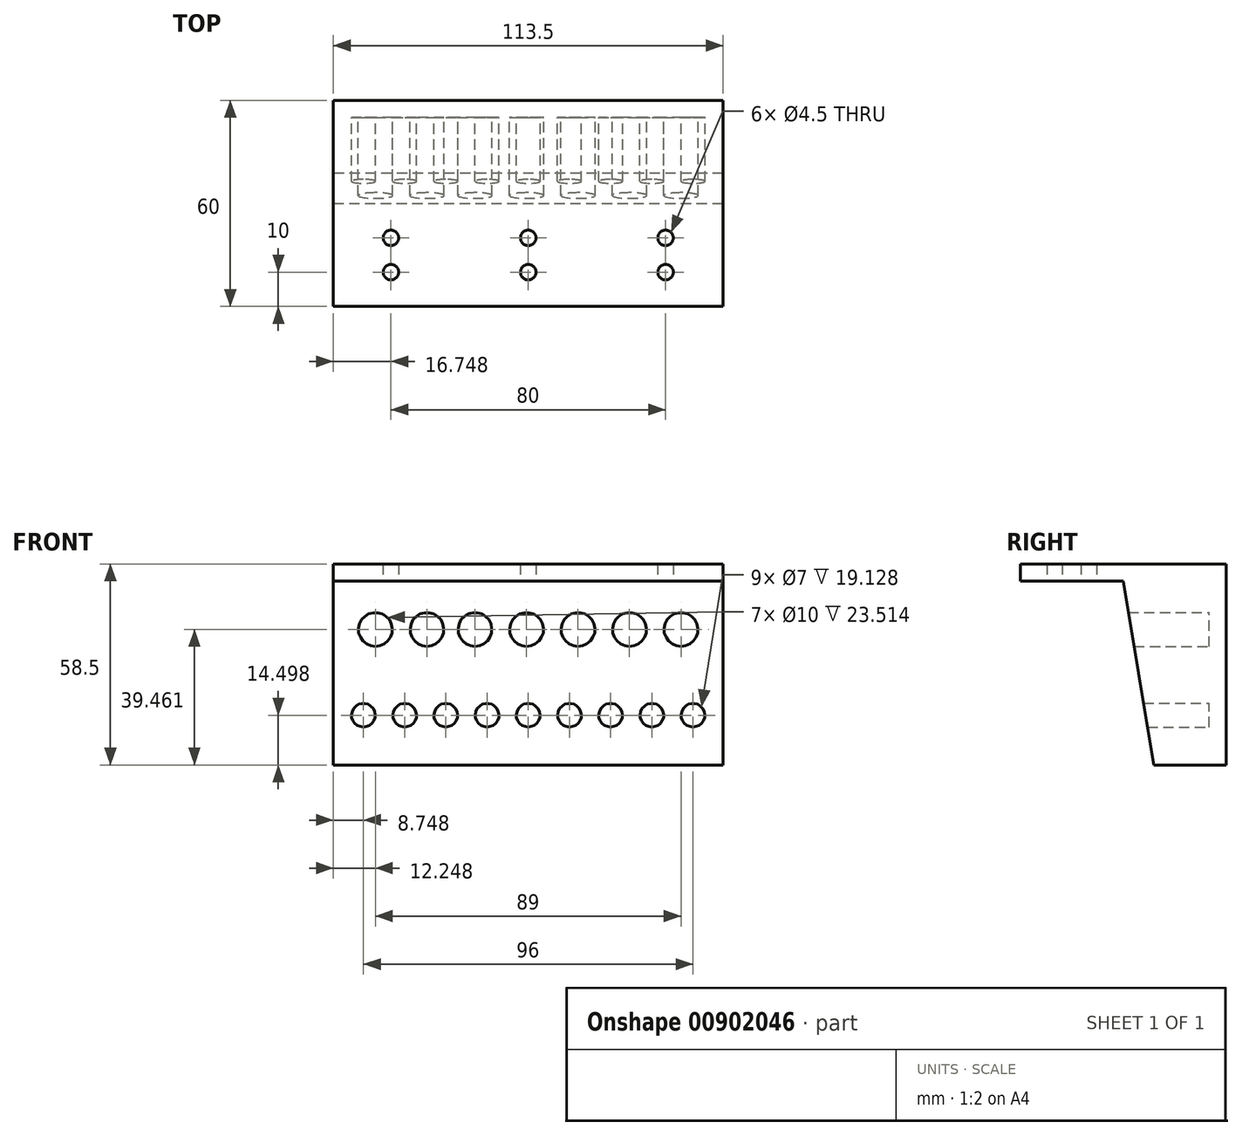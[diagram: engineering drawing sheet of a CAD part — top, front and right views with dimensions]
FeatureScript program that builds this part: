
annotation { "Feature Type Name" : "Feature", "Feature Type Description" : "" }
export const myFeature = defineFeature(function(context is Context, id is Id, definition is map)
    precondition{}
    {
        {
            var Q0;
            Q0=qCreatedBy(makeId("Front.planeOp"),FACE);
            var sketch = newSketch(context, id + "F0", { "sketchPlane" : qUnion([Q0])});
            skLineSegment(sketch, "E0.bottom", {"start": v(-82.73, 51.75) * mm, "end": v(30.77, 51.75) * mm});
            skLineSegment(sketch, "E0.top", {"start": v(-82.73, -1.75) * mm, "end": v(30.77, -1.75) * mm});
            skLineSegment(sketch, "E0.left", {"start": v(-82.73, 51.75) * mm, "end": v(-82.73, -1.75) * mm});
            skLineSegment(sketch, "E0.right", {"start": v(30.77, 51.75) * mm, "end": v(30.77, -1.75) * mm});
            skLineSegment(sketch, "E1", {"start": v(30.77, 37.71) * mm, "end": v(-82.73, 37.71) * mm});
            skLineSegment(sketch, "E2", {"start": v(-82.73, 37.71) * mm, "end": v(-82.73, 12.75) * mm});
            skLineSegment(sketch, "E3", {"start": v(-82.73, 12.75) * mm, "end": v(30.77, 12.75) * mm});
            skCircle(sketch, "E4", {"center": v(18.52, 37.71) * mm, "radius": 5 * mm});
            skCircle(sketch, "E5", {"center": v(3.52, 37.71) * mm, "radius": 5 * mm});
            skCircle(sketch, "E6", {"center": v(-11.48, 37.71) * mm, "radius": 5 * mm});
            skCircle(sketch, "E7", {"center": v(-26.48, 37.71) * mm, "radius": 5 * mm});
            skCircle(sketch, "E8", {"center": v(-41.48, 37.71) * mm, "radius": 5 * mm});
            skCircle(sketch, "E9", {"center": v(-55.48, 37.71) * mm, "radius": 5 * mm});
            skCircle(sketch, "E10", {"center": v(-70.48, 37.71) * mm, "radius": 5 * mm});
            skCircle(sketch, "E11", {"center": v(22.02, 12.75) * mm, "radius": 3.5 * mm});
            skCircle(sketch, "E12", {"center": v(10.02, 12.75) * mm, "radius": 3.5 * mm});
            skCircle(sketch, "E13", {"center": v(-1.98, 12.75) * mm, "radius": 3.5 * mm});
            skCircle(sketch, "E14", {"center": v(-13.98, 12.75) * mm, "radius": 3.5 * mm});
            skCircle(sketch, "E15", {"center": v(-25.98, 12.75) * mm, "radius": 3.5 * mm});
            skCircle(sketch, "E16", {"center": v(-37.98, 12.75) * mm, "radius": 3.5 * mm});
            skCircle(sketch, "E17", {"center": v(-49.98, 12.75) * mm, "radius": 3.5 * mm});
            skCircle(sketch, "E18", {"center": v(-61.98, 12.75) * mm, "radius": 3.5 * mm});
            skCircle(sketch, "E19", {"center": v(-73.98, 12.75) * mm, "radius": 3.5 * mm});
            skSolve(sketch);
        }
        {
            var Q0;
            {var subQ24=sQuery(id+"F0.wireOp",EDGE,"E0.left");var subQ32=sQuery(id+"F0.wireOp",EDGE,"E1");var subQ33=makeQuery(id+"F0.imprint","INTERSECT",VERTEX,{"derivedFrom":[subQ24,subQ32]});var subQ74=sQuery(id+"F0.wireOp",EDGE,"E0.top");var subQ75=sQuery(id+"F0.wireOp",EDGE,"E0.bottom");Q0=qUnion([makeQuery(id+"F0.imprint","IMPRINT",FACE,{"disambiguationData":[TD([[makeQuery(id+"F0.imprint","IMPRINT",EDGE,{"derivedFrom":subQ75}),-1.0]])]}),makeQuery(id+"F0.imprint","IMPRINT",FACE,{"disambiguationData":[TD([[makeQuery(id+"F0.imprint","IMPRINT",EDGE,{"derivedFrom":subQ74}),1.0]])]}),makeQuery(id+"F0.imprint","IMPRINT",FACE,{"disambiguationData":[TD([[makeQuery(id+"F0.imprint","IMPRINT",EDGE,{"disambiguationData":[TD([[subQ33,-1.0]])],"derivedFrom":subQ24}),1.0]])]})]);}
            extrude(context, id + "F1", {"entities" : qUnion([Q0]), "depth" : 25 * mm, "offsetDistance" : 25 * mm});
        }
        {
            var Q0;
            Q0=makeQuery(id+"F1.opExtrude","CAP_FACE",FACE,{"disambiguationData":[OSD([sQuery(id+"F0.wireOp",EDGE,"E0.bottom"),sQuery(id+"F0.wireOp",EDGE,"E0.top"),sQuery(id+"F0.wireOp",EDGE,"E0.left"),sQuery(id+"F0.wireOp",EDGE,"E0.right"),sQuery(id+"F0.wireOp",EDGE,"E4"),sQuery(id+"F0.wireOp",EDGE,"E5"),sQuery(id+"F0.wireOp",EDGE,"E6"),sQuery(id+"F0.wireOp",EDGE,"E7"),sQuery(id+"F0.wireOp",EDGE,"E8"),sQuery(id+"F0.wireOp",EDGE,"E9"),sQuery(id+"F0.wireOp",EDGE,"E10"),sQuery(id+"F0.wireOp",EDGE,"E11"),sQuery(id+"F0.wireOp",EDGE,"E12"),sQuery(id+"F0.wireOp",EDGE,"E13"),sQuery(id+"F0.wireOp",EDGE,"E14"),sQuery(id+"F0.wireOp",EDGE,"E15"),sQuery(id+"F0.wireOp",EDGE,"E16"),sQuery(id+"F0.wireOp",EDGE,"E17"),sQuery(id+"F0.wireOp",EDGE,"E18"),sQuery(id+"F0.wireOp",EDGE,"E19")])],"isStart":true});
            var sketch = newSketch(context, id + "F2", { "sketchPlane" : qUnion([Q0])});
            skLineSegment(sketch, "E20.bottom", {"start": v(-30.77, 51.75) * mm, "end": v(82.73, 51.75) * mm});
            skLineSegment(sketch, "E20.top", {"start": v(-30.77, -1.75) * mm, "end": v(82.73, -1.75) * mm});
            skLineSegment(sketch, "E20.left", {"start": v(-30.77, 51.75) * mm, "end": v(-30.77, -1.75) * mm});
            skLineSegment(sketch, "E20.right", {"start": v(82.73, 51.75) * mm, "end": v(82.73, -1.75) * mm});
            skSolve(sketch);
        }
        {
            var Q0;
            Q0=qSketchRegion(id+"F2",true);
            extrude(context, id + "F3", {"entities" : qUnion([Q0]), "operationType" : NewBodyOperationType.ADD, "depth" : 5 * mm, "offsetDistance" : 25 * mm});
        }
        {
            var Q0;
            Q0=makeQuery(id+"F3.boolean.opBoolean","MERGE",FACE,{"derivedFrom":[makeQuery(id+"F1.opExtrude","SWEPT_FACE",FACE,{"disambiguationData":[OSD([sQuery(id+"F0.wireOp",EDGE,"E0.left")])]}),makeQuery(id+"F3.opExtrude","SWEPT_FACE",FACE,{"disambiguationData":[OSD([sQuery(id+"F2.wireOp",EDGE,"E20.right")])]})]});
            var sketch = newSketch(context, id + "F4", { "sketchPlane" : qUnion([Q0])});
            skLineSegment(sketch, "E21", {"start": v(25, 51.75) * mm, "end": v(16.14, -1.75) * mm});
            skLineSegment(sketch, "E22", {"start": v(16.14, -1.75) * mm, "end": v(25, -1.75) * mm});
            skLineSegment(sketch, "E23", {"start": v(25, -1.75) * mm, "end": v(25, 51.75) * mm});
            skSolve(sketch);
        }
        {
            var Q0;
            Q0=qSketchRegion(id+"F4",true);
            extrude(context, id + "F5", {"entities" : qUnion([Q0]), "operationType" : NewBodyOperationType.REMOVE, "oppositeDirection" : true, "depth" : 133.9 * mm, "offsetDistance" : 25 * mm});
        }
        {
            var Q0;
            Q0=makeQuery(id+"F3.boolean.opBoolean","MERGE",FACE,{"derivedFrom":[makeQuery(id+"F1.opExtrude","SWEPT_FACE",FACE,{"disambiguationData":[OSD([sQuery(id+"F0.wireOp",EDGE,"E0.bottom")])]}),makeQuery(id+"F3.opExtrude","SWEPT_FACE",FACE,{"disambiguationData":[OSD([sQuery(id+"F2.wireOp",EDGE,"E20.bottom")])]})]});
            var sketch = newSketch(context, id + "F6", { "sketchPlane" : qUnion([Q0])});
            skLineSegment(sketch, "E24.bottom", {"start": v(30.77, 5) * mm, "end": v(-82.73, 5) * mm});
            skLineSegment(sketch, "E24.top", {"start": v(30.77, -55) * mm, "end": v(-82.73, -55) * mm});
            skLineSegment(sketch, "E24.left", {"start": v(30.77, 5) * mm, "end": v(30.77, -55) * mm});
            skLineSegment(sketch, "E24.right", {"start": v(-82.73, 5) * mm, "end": v(-82.73, -55) * mm});
            skSolve(sketch);
        }
        {
            var Q0;
            Q0=qSketchRegion(id+"F6",true);
            extrude(context, id + "F7", {"entities" : qUnion([Q0]), "operationType" : NewBodyOperationType.ADD, "depth" : 5 * mm, "offsetDistance" : 25 * mm});
        }
        {
            var Q0;
            Q0=makeQuery(id+"F7.opExtrude","CAP_FACE",FACE,{"disambiguationData":[OSD([sQuery(id+"F6.wireOp",EDGE,"E24.bottom"),sQuery(id+"F6.wireOp",EDGE,"E24.top"),sQuery(id+"F6.wireOp",EDGE,"E24.left"),sQuery(id+"F6.wireOp",EDGE,"E24.right")])],"isStart":true});
            var sketch = newSketch(context, id + "F8", { "sketchPlane" : qUnion([Q0])});
            skLineSegment(sketch, "E25", {"start": v(-82.73, 45) * mm, "end": v(30.77, 45) * mm});
            skLineSegment(sketch, "E26", {"start": v(-82.73, 35) * mm, "end": v(30.77, 35) * mm});
            skCircle(sketch, "E27", {"center": v(-65.98, 45) * mm, "radius": 2.25 * mm});
            skCircle(sketch, "E28", {"center": v(-25.98, 45) * mm, "radius": 2.25 * mm});
            skCircle(sketch, "E29", {"center": v(14.02, 45) * mm, "radius": 2.25 * mm});
            skCircle(sketch, "E30", {"center": v(-25.98, 35) * mm, "radius": 2.25 * mm});
            skCircle(sketch, "E31", {"center": v(-65.98, 35) * mm, "radius": 2.25 * mm});
            skCircle(sketch, "E32", {"center": v(14.02, 35) * mm, "radius": 2.25 * mm});
            skSolve(sketch);
        }
        {
            var Q0;
            Q0=qSketchRegion(id+"F8",true);
            extrude(context, id + "F9", {"entities" : qUnion([Q0]), "operationType" : NewBodyOperationType.REMOVE, "oppositeDirection" : true, "depth" : 25 * mm, "offsetDistance" : 25 * mm});
        }
    });
